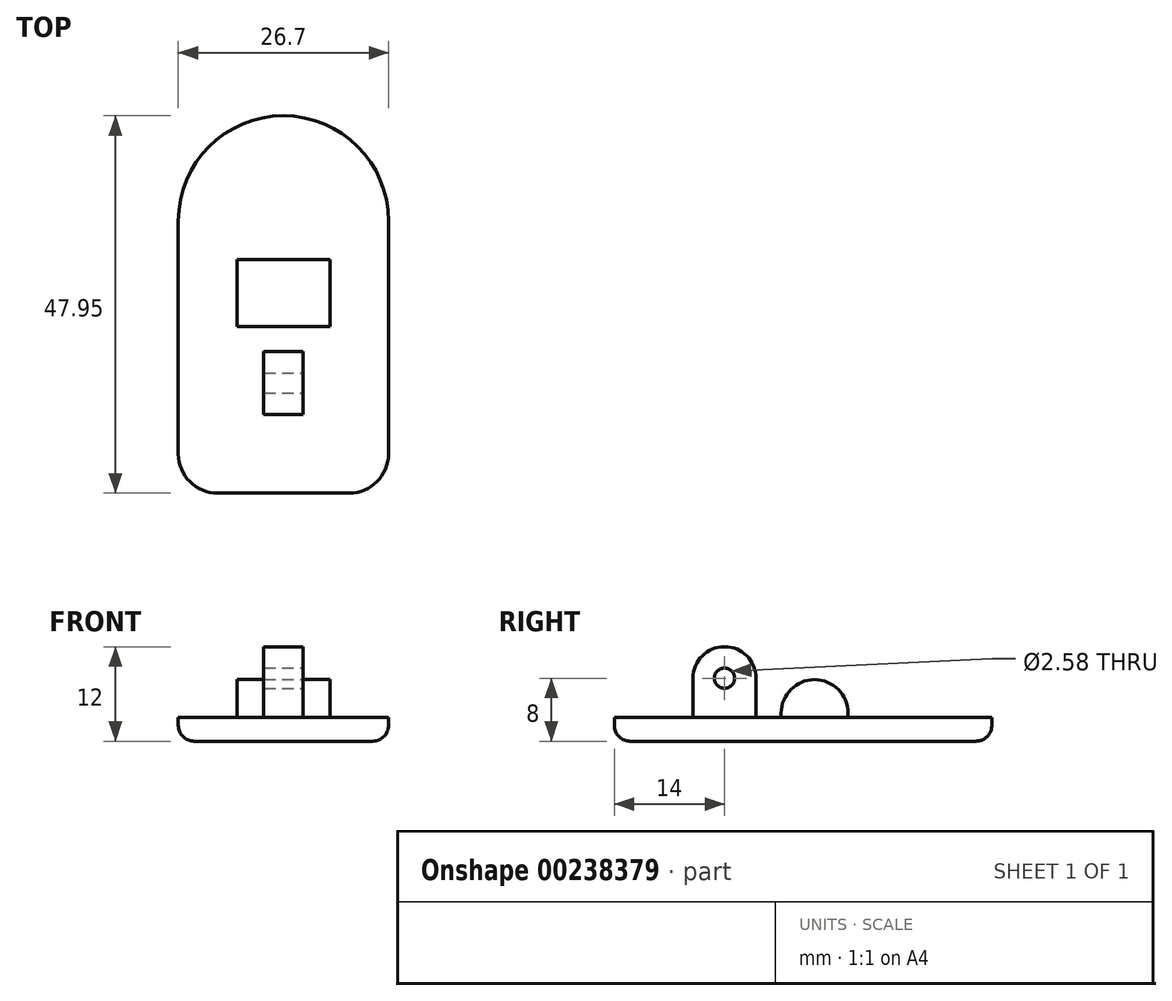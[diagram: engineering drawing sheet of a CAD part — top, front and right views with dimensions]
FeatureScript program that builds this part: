
annotation { "Feature Type Name" : "Feature", "Feature Type Description" : "" }
export const myFeature = defineFeature(function(context is Context, id is Id, definition is map)
    precondition{}
    {
        {
            var Q0;
            Q0=qCreatedBy(makeId("Top.planeOp"),FACE);
            var sketch = newSketch(context, id + "F0", { "sketchPlane" : qUnion([Q0])});
            skArc(sketch, "E0", {"start": v(13.35, 0) * mm, "mid": v(0, 13.35) * mm, "end": v(-13.35, 0) * mm});
            skLineSegment(sketch, "E1", {"start": v(-13.35, 0) * mm, "end": v(-13.35, -34.6) * mm});
            skLineSegment(sketch, "E2", {"start": v(13.35, 0) * mm, "end": v(13.35, -34.6) * mm});
            skLineSegment(sketch, "E3", {"start": v(13.35, -34.6) * mm, "end": v(-13.35, -34.6) * mm});
            skLineSegment(sketch, "E4", {"start": v(0, -34.6) * mm, "end": v(0, 13.35) * mm});
            skLineSegment(sketch, "E5", {"start": v(-13.35, -24.6) * mm, "end": v(13.35, -24.6) * mm});
            skLineSegment(sketch, "E6", {"start": v(-13.35, -16.6) * mm, "end": v(13.35, -16.6) * mm});
            skLineSegment(sketch, "E7", {"start": v(-2.5, -16.6) * mm, "end": v(-2.5, -34.6) * mm});
            skLineSegment(sketch, "E8", {"start": v(2.5, -16.6) * mm, "end": v(2.5, -34.6) * mm});
            skPoint(sketch, "E9.orphan", {"position": v(-2.5, 0) * mm});
            skPoint(sketch, "E10.orphan", {"position": v(2.5, 0) * mm});
            skLineSegment(sketch, "E11", {"start": v(-5.9, 0) * mm, "end": v(-5.9, -16.6) * mm});
            skLineSegment(sketch, "E12", {"start": v(5.9, 0) * mm, "end": v(5.9, -16.6) * mm});
            skLineSegment(sketch, "E13", {"start": v(-13.35, -4.9) * mm, "end": v(13.35, -4.9) * mm});
            skLineSegment(sketch, "E14", {"start": v(-13.35, -13.4) * mm, "end": v(13.35, -13.4) * mm});
            skSolve(sketch);
        }
        {
            var Q0;
            {var subQ4=sQuery(id+"F0.wireOp",EDGE,"E1");var subQ6=sQuery(id+"F0.wireOp",EDGE,"E5");var subQ7=makeQuery(id+"F0.imprint","INTERSECT",VERTEX,{"derivedFrom":[subQ4,subQ6]});Q0=makeQuery(id+"F0.imprint","IMPRINT",FACE,{"disambiguationData":[TD([[makeQuery(id+"F0.imprint","IMPRINT",EDGE,{"disambiguationData":[TD([[subQ7,1.0]])],"derivedFrom":subQ4}),1.0]])]});}
            var Q1;
            {var subQ0=sQuery(id+"F0.wireOp",EDGE,"E3");var subQ1=sQuery(id+"F0.wireOp",EDGE,"E1");var subQ2=makeQuery(id+"F0.imprint","INTERSECT",VERTEX,{"derivedFrom":[subQ1,subQ0]});Q1=makeQuery(id+"F0.imprint","IMPRINT",FACE,{"disambiguationData":[TD([[makeQuery(id+"F0.imprint","IMPRINT",EDGE,{"disambiguationData":[TD([[subQ2,1.0]])],"derivedFrom":subQ1}),1.0]])]});}
            var Q2;
            {var subQ0=sQuery(id+"F0.wireOp",EDGE,"E4");var subQ1=sQuery(id+"F0.wireOp",EDGE,"E3");var subQ2=makeQuery(id+"F0.imprint","INTERSECT",VERTEX,{"derivedFrom":[subQ1,subQ0]});Q2=makeQuery(id+"F0.imprint","IMPRINT",FACE,{"disambiguationData":[TD([[makeQuery(id+"F0.imprint","IMPRINT",EDGE,{"disambiguationData":[TD([[subQ2,1.0]])],"derivedFrom":subQ1}),-1.0]])]});}
            var Q3;
            {var subQ0=sQuery(id+"F0.wireOp",EDGE,"E4");var subQ1=sQuery(id+"F0.wireOp",EDGE,"E3");var subQ2=makeQuery(id+"F0.imprint","INTERSECT",VERTEX,{"derivedFrom":[subQ1,subQ0]});Q3=makeQuery(id+"F0.imprint","IMPRINT",FACE,{"disambiguationData":[TD([[makeQuery(id+"F0.imprint","IMPRINT",EDGE,{"disambiguationData":[TD([[subQ2,-1.0]])],"derivedFrom":subQ1}),-1.0]])]});}
            var Q4;
            {var subQ0=sQuery(id+"F0.wireOp",EDGE,"E5");var subQ1=sQuery(id+"F0.wireOp",EDGE,"E4");var subQ2=makeQuery(id+"F0.imprint","INTERSECT",VERTEX,{"derivedFrom":[subQ1,subQ0]});Q4=makeQuery(id+"F0.imprint","IMPRINT",FACE,{"disambiguationData":[TD([[makeQuery(id+"F0.imprint","IMPRINT",EDGE,{"disambiguationData":[TD([[subQ2,-1.0]])],"derivedFrom":subQ1}),1.0]])]});}
            var Q5;
            {var subQ0=sQuery(id+"F0.wireOp",EDGE,"E5");var subQ1=sQuery(id+"F0.wireOp",EDGE,"E4");var subQ2=makeQuery(id+"F0.imprint","INTERSECT",VERTEX,{"derivedFrom":[subQ1,subQ0]});Q5=makeQuery(id+"F0.imprint","IMPRINT",FACE,{"disambiguationData":[TD([[makeQuery(id+"F0.imprint","IMPRINT",EDGE,{"disambiguationData":[TD([[subQ2,-1.0]])],"derivedFrom":subQ1}),-1.0]])]});}
            var Q6;
            {var subQ1=sQuery(id+"F0.wireOp",EDGE,"E2");var subQ4=sQuery(id+"F0.wireOp",EDGE,"E5");var subQ5=makeQuery(id+"F0.imprint","INTERSECT",VERTEX,{"derivedFrom":[subQ1,subQ4]});Q6=makeQuery(id+"F0.imprint","IMPRINT",FACE,{"disambiguationData":[TD([[makeQuery(id+"F0.imprint","IMPRINT",EDGE,{"disambiguationData":[TD([[subQ5,1.0]])],"derivedFrom":subQ1}),-1.0]])]});}
            var Q7;
            {var subQ0=sQuery(id+"F0.wireOp",EDGE,"E3");var subQ1=sQuery(id+"F0.wireOp",EDGE,"E2");var subQ2=makeQuery(id+"F0.imprint","INTERSECT",VERTEX,{"derivedFrom":[subQ1,subQ0]});Q7=makeQuery(id+"F0.imprint","IMPRINT",FACE,{"disambiguationData":[TD([[makeQuery(id+"F0.imprint","IMPRINT",EDGE,{"disambiguationData":[TD([[subQ2,1.0]])],"derivedFrom":subQ1}),-1.0]])]});}
            var Q8;
            {var subQ0=sQuery(id+"F0.wireOp",EDGE,"E6");var subQ4=sQuery(id+"F0.wireOp",EDGE,"E4");var subQ5=makeQuery(id+"F0.imprint","INTERSECT",VERTEX,{"derivedFrom":[subQ4,subQ0]});Q8=makeQuery(id+"F0.imprint","IMPRINT",FACE,{"disambiguationData":[TD([[makeQuery(id+"F0.imprint","IMPRINT",EDGE,{"disambiguationData":[TD([[subQ5,-1.0]])],"derivedFrom":subQ4}),-1.0]])]});}
            var Q9;
            {var subQ0=sQuery(id+"F0.wireOp",EDGE,"E6");var subQ1=sQuery(id+"F0.wireOp",EDGE,"E2");var subQ2=makeQuery(id+"F0.imprint","INTERSECT",VERTEX,{"derivedFrom":[subQ1,subQ0]});Q9=makeQuery(id+"F0.imprint","IMPRINT",FACE,{"disambiguationData":[TD([[makeQuery(id+"F0.imprint","IMPRINT",EDGE,{"disambiguationData":[TD([[subQ2,1.0]])],"derivedFrom":subQ1}),-1.0]])]});}
            var Q10;
            {var subQ1=sQuery(id+"F0.wireOp",EDGE,"E6");var subQ6=sQuery(id+"F0.wireOp",EDGE,"E4");var subQ7=makeQuery(id+"F0.imprint","INTERSECT",VERTEX,{"derivedFrom":[subQ6,subQ1]});Q10=makeQuery(id+"F0.imprint","IMPRINT",FACE,{"disambiguationData":[TD([[makeQuery(id+"F0.imprint","IMPRINT",EDGE,{"disambiguationData":[TD([[subQ7,-1.0]])],"derivedFrom":subQ6}),1.0]])]});}
            var Q11;
            {var subQ0=sQuery(id+"F0.wireOp",EDGE,"E6");var subQ1=sQuery(id+"F0.wireOp",EDGE,"E1");var subQ2=makeQuery(id+"F0.imprint","INTERSECT",VERTEX,{"derivedFrom":[subQ1,subQ0]});Q11=makeQuery(id+"F0.imprint","IMPRINT",FACE,{"disambiguationData":[TD([[makeQuery(id+"F0.imprint","IMPRINT",EDGE,{"disambiguationData":[TD([[subQ2,1.0]])],"derivedFrom":subQ1}),1.0]])]});}
            var Q12;
            {var subQ0=sQuery(id+"F0.wireOp",EDGE,"E13");var subQ1=sQuery(id+"F0.wireOp",EDGE,"E1");var subQ2=makeQuery(id+"F0.imprint","INTERSECT",VERTEX,{"derivedFrom":[subQ1,subQ0]});Q12=makeQuery(id+"F0.imprint","IMPRINT",FACE,{"disambiguationData":[TD([[makeQuery(id+"F0.imprint","IMPRINT",EDGE,{"disambiguationData":[TD([[subQ2,-1.0]])],"derivedFrom":subQ1}),1.0]])]});}
            var Q13;
            {var subQ0=sQuery(id+"F0.wireOp",EDGE,"E14");var subQ1=sQuery(id+"F0.wireOp",EDGE,"E4");var subQ2=makeQuery(id+"F0.imprint","INTERSECT",VERTEX,{"derivedFrom":[subQ1,subQ0]});Q13=makeQuery(id+"F0.imprint","IMPRINT",FACE,{"disambiguationData":[TD([[makeQuery(id+"F0.imprint","IMPRINT",EDGE,{"disambiguationData":[TD([[subQ2,-1.0]])],"derivedFrom":subQ1}),1.0]])]});}
            var Q14;
            {var subQ0=sQuery(id+"F0.wireOp",EDGE,"E14");var subQ1=sQuery(id+"F0.wireOp",EDGE,"E4");var subQ2=makeQuery(id+"F0.imprint","INTERSECT",VERTEX,{"derivedFrom":[subQ1,subQ0]});Q14=makeQuery(id+"F0.imprint","IMPRINT",FACE,{"disambiguationData":[TD([[makeQuery(id+"F0.imprint","IMPRINT",EDGE,{"disambiguationData":[TD([[subQ2,-1.0]])],"derivedFrom":subQ1}),-1.0]])]});}
            var Q15;
            {var subQ0=sQuery(id+"F0.wireOp",EDGE,"E13");var subQ1=sQuery(id+"F0.wireOp",EDGE,"E2");var subQ2=makeQuery(id+"F0.imprint","INTERSECT",VERTEX,{"derivedFrom":[subQ1,subQ0]});Q15=makeQuery(id+"F0.imprint","IMPRINT",FACE,{"disambiguationData":[TD([[makeQuery(id+"F0.imprint","IMPRINT",EDGE,{"disambiguationData":[TD([[subQ2,-1.0]])],"derivedFrom":subQ1}),-1.0]])]});}
            var Q16;
            {var subQ4=sQuery(id+"F0.wireOp",EDGE,"E0");var subQ6=sQuery(id+"F0.wireOp",EDGE,"E2");var subQ7=makeQuery(id+"F0.imprint","INTERSECT",VERTEX,{"derivedFrom":[subQ4,subQ6]});Q16=makeQuery(id+"F0.imprint","IMPRINT",FACE,{"disambiguationData":[TD([[makeQuery(id+"F0.imprint","IMPRINT",EDGE,{"disambiguationData":[TD([[subQ7,-1.0]])],"derivedFrom":subQ4}),1.0]])]});}
            var Q17;
            {var subQ1=sQuery(id+"F0.wireOp",EDGE,"E0");var subQ5=sQuery(id+"F0.wireOp",EDGE,"E1");var subQ8=makeQuery(id+"F0.imprint","INTERSECT",VERTEX,{"derivedFrom":[subQ1,subQ5]});Q17=makeQuery(id+"F0.imprint","IMPRINT",FACE,{"disambiguationData":[TD([[makeQuery(id+"F0.imprint","IMPRINT",EDGE,{"disambiguationData":[TD([[subQ8,1.0]])],"derivedFrom":subQ1}),1.0]])]});}
            extrude(context, id + "F1", {"entities" : qUnion([Q0, Q1, Q2, Q3, Q4, Q5, Q6, Q7, Q8, Q9, Q10, Q11, Q12, Q13, Q14, Q15, Q16, Q17]), "oppositeDirection" : true, "depth" : 3 * mm});
        }
        {
            var Q0;
            {var subQ0=sQuery(id+"F0.wireOp",EDGE,"E14");var subQ1=sQuery(id+"F0.wireOp",EDGE,"E4");var subQ2=makeQuery(id+"F0.imprint","INTERSECT",VERTEX,{"derivedFrom":[subQ1,subQ0]});Q0=makeQuery(id+"F0.imprint","IMPRINT",FACE,{"disambiguationData":[TD([[makeQuery(id+"F0.imprint","IMPRINT",EDGE,{"disambiguationData":[TD([[subQ2,-1.0]])],"derivedFrom":subQ1}),1.0]])]});}
            var Q1;
            {var subQ0=sQuery(id+"F0.wireOp",EDGE,"E14");var subQ1=sQuery(id+"F0.wireOp",EDGE,"E4");var subQ2=makeQuery(id+"F0.imprint","INTERSECT",VERTEX,{"derivedFrom":[subQ1,subQ0]});Q1=makeQuery(id+"F0.imprint","IMPRINT",FACE,{"disambiguationData":[TD([[makeQuery(id+"F0.imprint","IMPRINT",EDGE,{"disambiguationData":[TD([[subQ2,-1.0]])],"derivedFrom":subQ1}),-1.0]])]});}
            extrude(context, id + "F2", {"entities" : qUnion([Q0, Q1]), "operationType" : NewBodyOperationType.ADD, "depth" : .563 * mm});
        }
        {
            var Q0;
            {var subQ0=sQuery(id+"F0.wireOp",EDGE,"E5");var subQ1=sQuery(id+"F0.wireOp",EDGE,"E4");var subQ2=makeQuery(id+"F0.imprint","INTERSECT",VERTEX,{"derivedFrom":[subQ1,subQ0]});Q0=makeQuery(id+"F0.imprint","IMPRINT",FACE,{"disambiguationData":[TD([[makeQuery(id+"F0.imprint","IMPRINT",EDGE,{"disambiguationData":[TD([[subQ2,-1.0]])],"derivedFrom":subQ1}),-1.0]])]});}
            var Q1;
            {var subQ0=sQuery(id+"F0.wireOp",EDGE,"E5");var subQ1=sQuery(id+"F0.wireOp",EDGE,"E4");var subQ2=makeQuery(id+"F0.imprint","INTERSECT",VERTEX,{"derivedFrom":[subQ1,subQ0]});Q1=makeQuery(id+"F0.imprint","IMPRINT",FACE,{"disambiguationData":[TD([[makeQuery(id+"F0.imprint","IMPRINT",EDGE,{"disambiguationData":[TD([[subQ2,-1.0]])],"derivedFrom":subQ1}),1.0]])]});}
            extrude(context, id + "F3", {"entities" : qUnion([Q0, Q1]), "operationType" : NewBodyOperationType.ADD, "depth" : 5 * mm});
        }
        {
            var Q0;
            Q0=makeQuery(id+"F3.opExtrude","SWEPT_FACE",FACE,{"disambiguationData":[OSD([sQuery(id+"F0.wireOp",EDGE,"E8")])]});
            var sketch = newSketch(context, id + "F4", { "sketchPlane" : qUnion([Q0])});
            skCircle(sketch, "E15", {"center": v(-20.6, 5) * mm, "radius": 4 * mm});
            skCircle(sketch, "E16", {"center": v(-20.6, 5) * mm, "radius": 1.29 * mm});
            skSolve(sketch);
        }
        {
            var Q0;
            Q0=makeQuery(id+"F2.opExtrude","SWEPT_FACE",FACE,{"disambiguationData":[OSD([sQuery(id+"F0.wireOp",EDGE,"E12")])]});
            var sketch = newSketch(context, id + "F5", { "sketchPlane" : qUnion([Q0])});
            skCircle(sketch, "E17", {"center": v(-9.15, 0.56) * mm, "radius": 4.25 * mm});
            skSolve(sketch);
        }
        {
            var Q0;
            {var subQ1=sQuery(id+"F0.wireOp",EDGE,"E12");var subQ2=makeQuery(id+"F2.opExtrude","CAP_EDGE",EDGE,{"disambiguationData":[OSD([subQ1])],"isStart":false});Q0=makeQuery(id+"F5.imprint","IMPRINT",FACE,{"disambiguationData":[TD([[makeQuery(id+"F5.imprint","IMPRINT",EDGE,{"derivedFrom":subQ2}),-1.0]])]});}
            extrude(context, id + "F6", {"entities" : qUnion([Q0]), "operationType" : NewBodyOperationType.ADD, "oppositeDirection" : true, "depth" : 11.8 * mm});
        }
        {
            var Q0;
            {var subQ1=sQuery(id+"F0.wireOp",EDGE,"E8");var subQ2=makeQuery(id+"F3.opExtrude","CAP_EDGE",EDGE,{"disambiguationData":[OSD([subQ1])],"isStart":false});Q0=makeQuery(id+"F4.imprint","IMPRINT",FACE,{"disambiguationData":[TD([[makeQuery(id+"F4.imprint","IMPRINT",EDGE,{"derivedFrom":subQ2}),-1.0]])]});}
            extrude(context, id + "F7", {"entities" : qUnion([Q0]), "operationType" : NewBodyOperationType.ADD, "oppositeDirection" : true, "depth" : 5 * mm});
        }
        {
            var Q0;
            {var subQ0=sQuery(id+"F4.wireOp",EDGE,"E16");var subQ1=makeQuery(id+"F3.opExtrude","CAP_EDGE",EDGE,{"disambiguationData":[OSD([sQuery(id+"F0.wireOp",EDGE,"E8")])],"isStart":false});var subQ2=makeQuery(id+"F4.imprint","INTERSECT",VERTEX,{"disambiguationData":[OD(0.0)],"derivedFrom":[subQ1,subQ0]});Q0=makeQuery(id+"F4.imprint","IMPRINT",FACE,{"disambiguationData":[TD([[makeQuery(id+"F4.imprint","IMPRINT",EDGE,{"disambiguationData":[TD([[subQ2,1.0]])],"derivedFrom":subQ0}),1.0]])]});}
            var Q1;
            {var subQ0=sQuery(id+"F4.wireOp",EDGE,"E16");var subQ1=makeQuery(id+"F3.opExtrude","CAP_EDGE",EDGE,{"disambiguationData":[OSD([sQuery(id+"F0.wireOp",EDGE,"E8")])],"isStart":false});var subQ2=makeQuery(id+"F4.imprint","INTERSECT",VERTEX,{"disambiguationData":[OD(0.0)],"derivedFrom":[subQ1,subQ0]});Q1=makeQuery(id+"F4.imprint","IMPRINT",FACE,{"disambiguationData":[TD([[makeQuery(id+"F4.imprint","IMPRINT",EDGE,{"disambiguationData":[TD([[subQ2,-1.0]])],"derivedFrom":subQ0}),1.0]])]});}
            extrude(context, id + "F8", {"entities" : qUnion([Q0, Q1]), "operationType" : NewBodyOperationType.REMOVE, "oppositeDirection" : true, "depth" : 25 * mm});
        }
        {
            var Q0;
            {var subQ0=sQuery(id+"F0.wireOp",EDGE,"E8");Q0=makeQuery(id+"F7.boolean.opBoolean","MERGE",FACE,{"derivedFrom":[makeQuery(id+"F3.opExtrude","SWEPT_FACE",FACE,{"disambiguationData":[OSD([subQ0])]}),makeQuery(id+"F7.opExtrude","CAP_FACE",FACE,{"disambiguationData":[OSD([subQ0,sQuery(id+"F4.wireOp",EDGE,"E15"),sQuery(id+"F4.wireOp",EDGE,"E16")])],"isStart":true})]});}
            var sketch = newSketch(context, id + "F9", { "sketchPlane" : qUnion([Q0])});
            skCircle(sketch, "E18", {"center": v(-20.6, 5) * mm, "radius": 2.06 * mm});
            skSolve(sketch);
        }
        {
            var Q0;
            Q0=qSketchRegion(id+"F9",true);
            extrude(context, id + "F10", {"entities" : qUnion([Q0]), "operationType" : NewBodyOperationType.ADD, "oppositeDirection" : true, "depth" : 1 * mm});
        }
        {
            var Q0;
            Q0=makeQuery(id+"F1.opExtrude","SWEPT_EDGE",EDGE,{"disambiguationData":[OSD([sQuery(id+"F0.wireOp",EDGE,"E2"),sQuery(id+"F0.wireOp",EDGE,"E3")])]});
            fillet(context, id + "F11", {"entities" : qUnion([Q0]), "radius" : 5 * mm, "tangentPropagation" : true, "allowEdgeOverflow" : false});
        }
        {
            var Q0;
            Q0=makeQuery(id+"F1.opExtrude","SWEPT_EDGE",EDGE,{"disambiguationData":[OSD([sQuery(id+"F0.wireOp",EDGE,"E1"),sQuery(id+"F0.wireOp",EDGE,"E3")])]});
            fillet(context, id + "F12", {"entities" : qUnion([Q0]), "radius" : 5 * mm, "tangentPropagation" : true, "allowEdgeOverflow" : false});
        }
        {
            var Q0;
            Q0=makeQuery(id+"F1.opExtrude","CAP_EDGE",EDGE,{"disambiguationData":[OSD([sQuery(id+"F0.wireOp",EDGE,"E3")])],"isStart":false});
            fillet(context, id + "F13", {"entities" : qUnion([Q0]), "radius" : 2 * mm, "tangentPropagation" : true, "allowEdgeOverflow" : false});
        }
        {
            var Q0;
            Q0=makeQuery(id+"F10.opExtrude","CAP_FACE",FACE,{"disambiguationData":[OSD([sQuery(id+"F9.wireOp",EDGE,"E18")])],"isStart":false});
            extrude(context, id + "F14", {"entities" : qUnion([Q0]), "operationType" : NewBodyOperationType.REMOVE, "oppositeDirection" : true, "depth" : 25 * mm});
        }
    });
